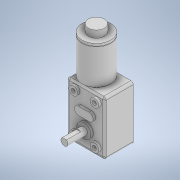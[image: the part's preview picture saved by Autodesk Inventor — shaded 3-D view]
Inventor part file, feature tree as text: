
AUTODESK INVENTOR PART (.ipt)
format: ipt  version: 2020 (Build 240168000, 168)  size: 299,008 bytes
history: native  units: mm
features: sketch x8, extrude x7, projected_geometry x7, fillet x3, chamfer x2, hole x1, plane x1, split x1
ambient origin geometry x8: Origin, YZ Plane, XZ Plane, XY Plane, X Axis, Y Axis, Z Axis, Center Point
bodies: Solid1 (feature_tree), Solid2 (feature_tree), Solid3 (feature_tree), Solid4 (feature_tree)
feature tree (30):
  extrude  "Extrusion1"  Depth=25.0mm
  extrude  "Extrusion3"  Depth=46.0mm
  extrude  "Extrusion4"  Depth=30.8mm
  extrude  "Extrusion5"  Depth=32.0mm
  hole  "Hole1"  [1 undecoded]
  fillet  "Fillet1"  Radius=12.0mm
  chamfer  "Chamfer9"  Distance=15.0mm
  chamfer  "Chamfer10"  Distance=7.0mm
  extrude  "Extrusion2"  Depth=7.0mm
  extrude  "Extrusion6"  Depth=2.0mm TaperAngle=0.0deg
  extrude  "Extrusion7"  Depth=6.0mm
  plane  "Work Plane1"
  split  "Split1"
  fillet  "Fillet2"  Radius=16.5mm
  fillet  "Fillet3"  Radius=12.0mm
  sketch  "Sketch1"  dims[d0=32.0mm d1=25.0mm]
  sketch  "Sketch2"  dims[d2=46.0mm d3=0.0mm d4=24.4mm]
  projected_geometry  "Projected Loop1"
  sketch  "Sketch3"  dims[d5=30.8mm d6=0.0mm d7=7.4mm]
  projected_geometry  "Projected Loop2"
  sketch  "Sketch4"  dims[d8=6.0mm d9=32.0mm]
  projected_geometry  "Projected Loop3"
  sketch  "Sketch5"  dims[d11=20.0mm d13=18.0mm d14=20.0mm d16=33.0mm d19=3.3mm d20=12.0mm]
  projected_geometry  "Projected Loop4"
  sketch  "Sketch6"  dims[d21=15.0mm]
  projected_geometry  "Projected Loop5"
  sketch  "Sketch7"  dims[d22=16.0mm]
  projected_geometry  "Projected Loop6"
  sketch  "Sketch8"  dims[d23=7.0mm d24=15.0mm d25=7.0mm d26=7.0mm d27=2.0mm d28=0.0mm d29=6.0mm d30=16.5mm d31=0.0mm d33=12.0mm d34=0.0mm d35=5.4mm d36=20.0mm d38=18.0mm d39=20.0mm d41=33.0mm d44=3.4mm d45=6.0mm d46=11.0mm d47=2.6mm d48=90.0deg d49=4.0mm d50=20.594885mm d51=2.0mm d52=0.0mm d53=13.5mm d54=6.0mm d55=0.0mm d80=2.0mm d81=1.0mm d82=2.0mm d83=45.0deg d84=1.0mm d85=2.0mm d86=45.0deg d87=0.5mm d88=0.5mm]
  projected_geometry  "Projected Loop7"
note: 1 required parameter value undecoded (feature->parameter linkage not recoverable at this tier; creation-order binding heuristic only, values carry confidence <= 0.55)
